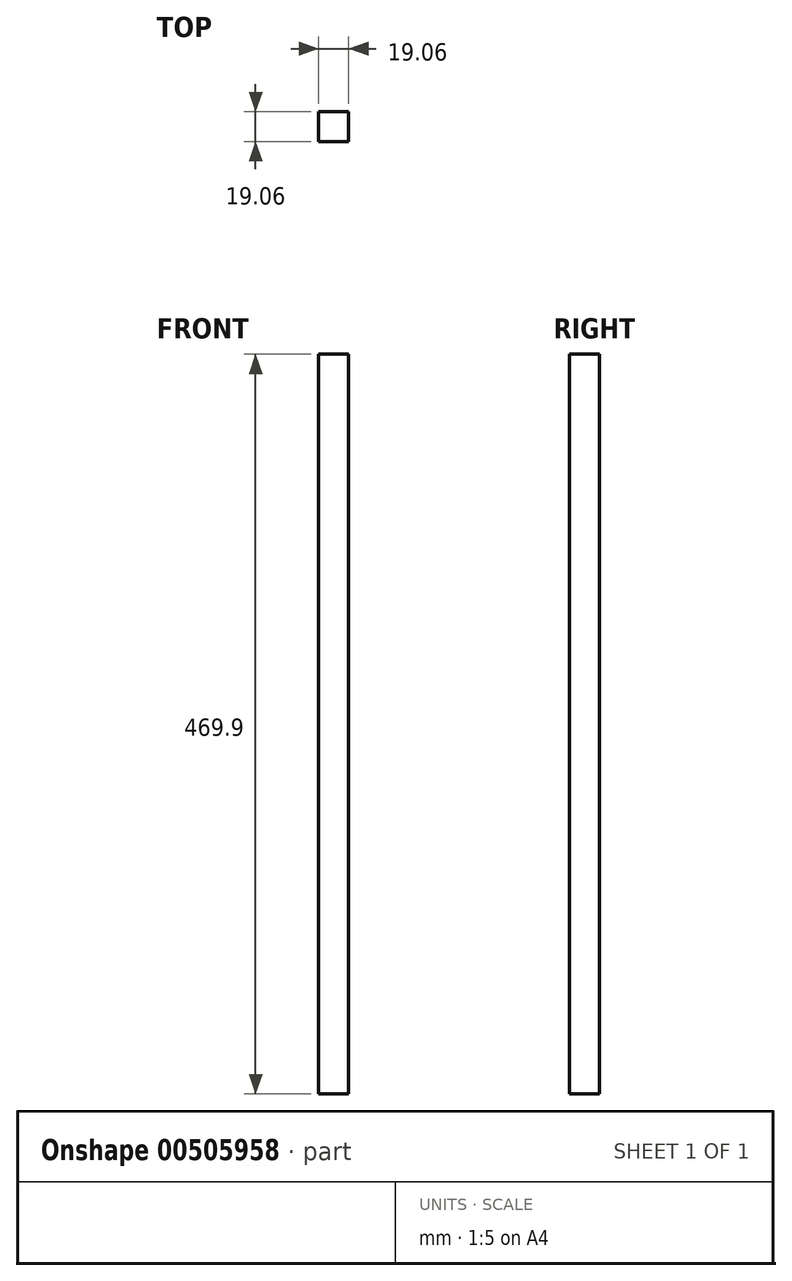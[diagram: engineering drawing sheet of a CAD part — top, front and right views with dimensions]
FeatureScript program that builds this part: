
annotation { "Feature Type Name" : "Feature", "Feature Type Description" : "" }
export const myFeature = defineFeature(function(context is Context, id is Id, definition is map)
    precondition{}
    {
        {
            var Q0;
            Q0=qCreatedBy(makeId("Top.planeOp"),FACE);
            var sketch = newSketch(context, id + "F0", { "sketchPlane" : qUnion([Q0])});
            skLineSegment(sketch, "E0.bottom", {"start": v(-9.53, 9.53) * mm, "end": v(9.53, 9.53) * mm});
            skLineSegment(sketch, "E0.top", {"start": v(-9.53, -9.53) * mm, "end": v(9.52, -9.53) * mm});
            skLineSegment(sketch, "E0.left", {"start": v(-9.53, 9.53) * mm, "end": v(-9.53, -9.53) * mm});
            skLineSegment(sketch, "E0.right", {"start": v(9.53, 9.53) * mm, "end": v(9.52, -9.53) * mm});
            skPoint(sketch, "E0.middle", {"position": v(0, 0) * mm});
            skSolve(sketch);
        }
        {
            var Q0;
            Q0=qSketchRegion(id+"F0",true);
            extrude(context, id + "F1", {"entities" : qUnion([Q0]), "depth" : 469.9 * mm, "offsetDistance" : 25.4 * mm});
        }
    });
